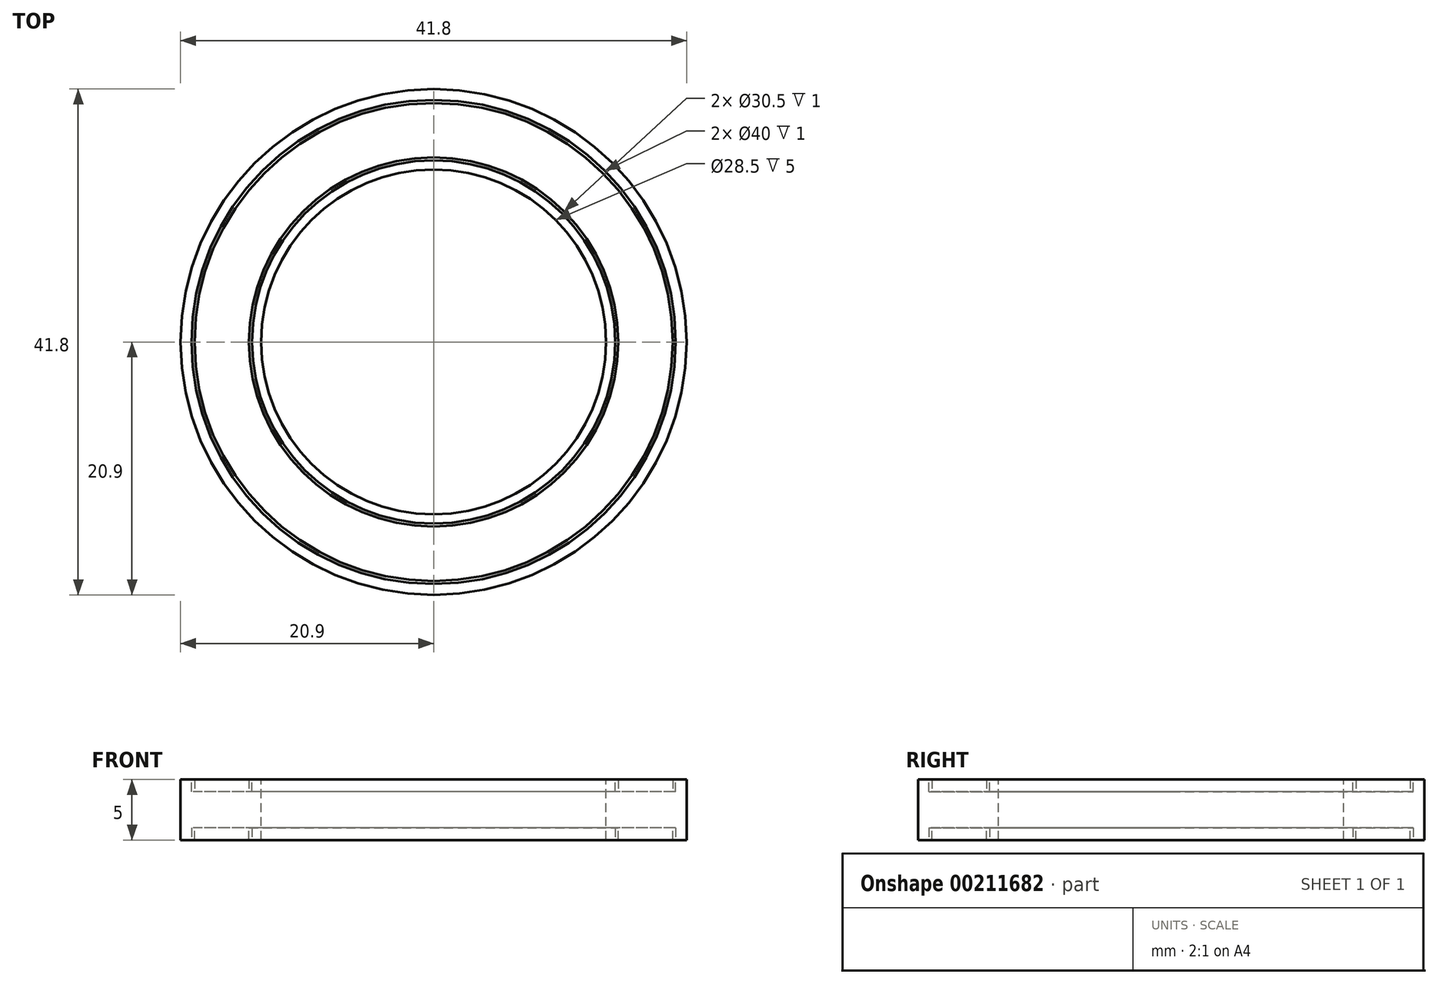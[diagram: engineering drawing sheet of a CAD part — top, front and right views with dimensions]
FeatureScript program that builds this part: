
annotation { "Feature Type Name" : "Feature", "Feature Type Description" : "" }
export const myFeature = defineFeature(function(context is Context, id is Id, definition is map)
    precondition{}
    {
        {
            var Q0;
            Q0=qCreatedBy(makeId("Top.planeOp"),FACE);
            var sketch = newSketch(context, id + "F0", { "sketchPlane" : qUnion([Q0])});
            skCircle(sketch, "E0", {"center": v(0, 0) * mm, "radius": 20.9 * mm});
            skSolve(sketch);
        }
        {
            var Q0;
            Q0=makeQuery(id+"F0.imprint","IMPRINT",FACE,{"disambiguationData":[TD([[makeQuery(id+"F0.imprint","IMPRINT",EDGE,{"derivedFrom":sQuery(id+"F0.wireOp",EDGE,"E0")}),1.0]])]});
            extrude(context, id + "F1", {"entities" : qUnion([Q0]), "depth" : 5 * mm});
        }
        {
            var Q0;
            Q0=makeQuery(id+"F1.opExtrude","CAP_FACE",FACE,{"disambiguationData":[OSD([sQuery(id+"F0.wireOp",EDGE,"E0")])],"isStart":false});
            var sketch = newSketch(context, id + "F2", { "sketchPlane" : qUnion([Q0])});
            skCircle(sketch, "E1", {"center": v(0, 0) * mm, "radius": 14.25 * mm});
            skSolve(sketch);
        }
        {
            var Q0;
            Q0=makeQuery(id+"F2.imprint","IMPRINT",FACE,{"disambiguationData":[TD([[makeQuery(id+"F2.imprint","IMPRINT",EDGE,{"derivedFrom":sQuery(id+"F2.wireOp",EDGE,"E1")}),1.0]])]});
            extrude(context, id + "F3", {"entities" : qUnion([Q0]), "operationType" : NewBodyOperationType.REMOVE, "oppositeDirection" : true, "depth" : 25 * mm});
        }
        {
            var Q0;
            Q0=makeQuery(id+"F1.opExtrude","CAP_FACE",FACE,{"disambiguationData":[OSD([sQuery(id+"F0.wireOp",EDGE,"E0")])],"isStart":false});
            var sketch = newSketch(context, id + "F4", { "sketchPlane" : qUnion([Q0])});
            skCircle(sketch, "E2", {"center": v(0, 0) * mm, "radius": 20 * mm});
            skCircle(sketch, "E3", {"center": v(0, 0) * mm, "radius": 15 * mm});
            skSolve(sketch);
        }
        {
            var Q0;
            Q0=makeQuery(id+"F4.imprint","IMPRINT",FACE,{"disambiguationData":[TD([[makeQuery(id+"F4.imprint","IMPRINT",EDGE,{"derivedFrom":sQuery(id+"F4.wireOp",EDGE,"E2")}),1.0]])]});
            extrude(context, id + "F5", {"entities" : qUnion([Q0]), "operationType" : NewBodyOperationType.REMOVE, "oppositeDirection" : true, "depth" : 1 * mm});
        }
        {
            var Q0;
            Q0=makeQuery(id+"F5.boolean.opBoolean","COPY",FACE,{"derivedFrom":makeQuery(id+"F5.opExtrude","CAP_FACE",FACE,{"disambiguationData":[OSD([sQuery(id+"F4.wireOp",EDGE,"E2"),sQuery(id+"F4.wireOp",EDGE,"E3")])],"isStart":false})});
            var sketch = newSketch(context, id + "F6", { "sketchPlane" : qUnion([Q0])});
            skCircle(sketch, "E4", {"center": v(0, 0) * mm, "radius": 15.25 * mm});
            skCircle(sketch, "E5", {"center": v(0, 0) * mm, "radius": 19.75 * mm});
            skSolve(sketch);
        }
        {
            var Q0;
            Q0=makeQuery(id+"F6.imprint","IMPRINT",FACE,{"disambiguationData":[TD([[makeQuery(id+"F6.imprint","IMPRINT",EDGE,{"derivedFrom":sQuery(id+"F6.wireOp",EDGE,"E4")}),-1.0]])]});
            extrude(context, id + "F7", {"entities" : qUnion([Q0]), "depth" : 1 * mm});
        }
        {
            var Q0;
            Q0=makeQuery(id+"F1.opExtrude","CAP_FACE",FACE,{"disambiguationData":[OSD([sQuery(id+"F0.wireOp",EDGE,"E0")])],"isStart":true});
            var sketch = newSketch(context, id + "F8", { "sketchPlane" : qUnion([Q0])});
            skCircle(sketch, "E6", {"center": v(0, 0) * mm, "radius": 29.89 * mm});
            skSolve(sketch);
        }
        {
            var Q0;
            {var subQ0=sQuery(id+"F0.wireOp",EDGE,"E0");Q0=makeQuery(id+"F8.imprint","IMPRINT",FACE,{"disambiguationData":[TD([[makeQuery(id+"F8.imprint","IMPRINT",EDGE,{"derivedFrom":makeQuery(id+"F1.opExtrude","CAP_EDGE",EDGE,{"disambiguationData":[OSD([subQ0])],"isStart":true})}),-1.0]])]});}
            extrude(context, id + "F9", {"entities" : qUnion([Q0]), "operationType" : NewBodyOperationType.REMOVE, "oppositeDirection" : true, "depth" : 2.5 * mm});
        }
        {
            var Q0;
            Q0=makeQuery(id+"F7.opExtrude","SWEPT_BODY",BODY,{"disambiguationData":[OSD([sQuery(id+"F6.wireOp",EDGE,"E4"),sQuery(id+"F6.wireOp",EDGE,"E5")])]});
            var Q1;
            Q1=makeQuery(id+"F9.boolean.opBoolean","COPY",FACE,{"derivedFrom":makeQuery(id+"F9.opExtrude","CAP_FACE",FACE,{"disambiguationData":[OSD([sQuery(id+"F0.wireOp",EDGE,"E0"),sQuery(id+"F2.wireOp",EDGE,"E1")])],"isStart":false})});
            mirror(context, id + "F10", {"entities" : qUnion([Q0]), "mirrorPlane" : qUnion([Q1])});
        }
        {
            var Q0;
            Q0=makeQuery(id+"F1.opExtrude","SWEPT_BODY",BODY,{"disambiguationData":[OSD([sQuery(id+"F0.wireOp",EDGE,"E0")])]});
            var Q1;
            Q1=makeQuery(id+"F9.boolean.opBoolean","COPY",FACE,{"derivedFrom":makeQuery(id+"F9.opExtrude","CAP_FACE",FACE,{"disambiguationData":[OSD([sQuery(id+"F0.wireOp",EDGE,"E0"),sQuery(id+"F2.wireOp",EDGE,"E1")])],"isStart":false})});
            mirror(context, id + "F11", {"operationType" : NewBodyOperationType.ADD, "entities" : qUnion([Q0]), "mirrorPlane" : qUnion([Q1])});
        }
    });
